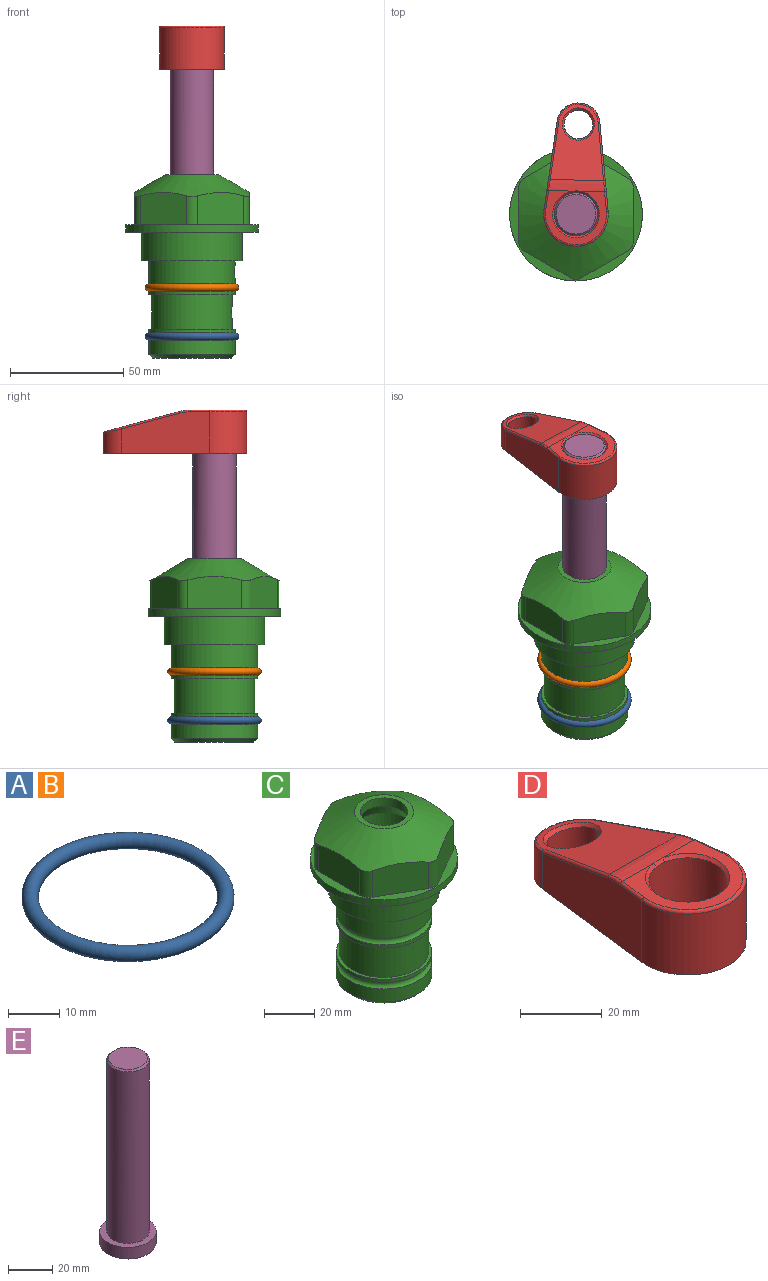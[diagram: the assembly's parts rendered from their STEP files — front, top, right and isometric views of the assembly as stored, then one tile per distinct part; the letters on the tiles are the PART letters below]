
ASSEMBLY  parts=5 mates=4
PART A: 1 faces, bbox 44.7x44.7x3.2 mm
  f0: torus R=19.05mm, axis (0,0,1), area 1193.9mm2
PART B: same geometry as A
PART C: 36 faces, bbox 58.7x58.7x81 mm
  f0: cylinder r=17.78mm len=35.56mm, axis (0,0,1), area 1670.8mm2, adj f23,f24,f31
  f1: cylinder r=19.05mm len=38.1mm, axis (0,0,1), area 1191.9mm2, adj f26,f27,f30
  f2: plane 58.66x58.66mm, normal (0,0,-1), area 1150.6mm2, adj f3,f28
  f3: cylinder r=29.33mm len=58.66mm, axis (0,0,-1), area 585.1mm2, adj f2,f4
  f4: plane 58.66x58.66mm, normal (0,0,1), area 475.9mm2, adj f3,f5,f6,f7,f8,f9,f10,f11
  f5: plane 20.32x14.34mm, normal (-0.5,0.87,0), area 324.4mm2, adj f4,f15,f16,f17
  f6: plane 20.32x14.34mm, normal (0.5,0.87,0), area 324.4mm2, adj f4,f14,f15,f17
  f7: plane 23.48x14.34mm, normal (1,0,0), area 324.4mm2, adj f4,f13,f14,f17
  f8: plane 20.32x14.34mm, normal (0.5,-0.87,0), area 324.4mm2, adj f4,f12,f13,f17
  f9: plane 20.32x14.34mm, normal (-0.5,-0.87,0), area 324.4mm2, adj f4,f11,f12,f17
  f10: plane 23.48x14.34mm, normal (-1,0,0), area 324.4mm2, adj f4,f11,f16,f17
  f11: cylinder r=5.08mm len=12.85mm, axis (0,0,-1), area 67.2mm2, adj f4,f9,f10,f17
  f12: cylinder r=5.08mm len=12.85mm, axis (0,0,-1), area 67.2mm2, adj f4,f8,f9,f17
  f13: cylinder r=5.08mm len=12.85mm, axis (0,0,-1), area 67.2mm2, adj f4,f7,f8,f17
  f14: cylinder r=5.08mm len=12.85mm, axis (0,0,-1), area 67.2mm2, adj f4,f6,f7,f17
  f15: cylinder r=5.08mm len=12.85mm, axis (0,0,-1), area 67.2mm2, adj f4,f5,f6,f17
  f16: cylinder r=5.08mm len=12.85mm, axis (0,0,-1), area 67.2mm2, adj f4,f5,f10,f17
  f17: cone r=11.73mm half-angle=60deg, axis (0,0,-1), area 2071.8mm2, adj f5,f6,f7,f8,f9,f10,f11,f12
  f18: plane 23.46x23.46mm, normal (0,0,1), area 147.4mm2, adj f17,f35
  f19: plane 34.93x34.93mm, normal (0,0,-1), area 958mm2, adj f29
  f20: cylinder r=19.05mm len=38.1mm, axis (0,0,1), area 760.1mm2, adj f21,f29
  f21: torus R=19.05mm, axis (0,0,1), area 565.3mm2, adj f20,f22
  f22: cylinder r=19.05mm len=38.1mm, axis (0,0,1), area 190mm2, adj f21,f23
  f23: plane 38.1x38.1mm, normal (0,0,1), area 146.9mm2, adj f0,f22
  f24: plane 38.1x38.1mm, normal (0,0,-1), area 146.9mm2, adj f0,f25
  f25: cylinder r=19.05mm len=38.1mm, axis (0,0,1), area 190mm2, adj f24,f26
  f26: torus R=19.05mm, axis (0,0,1), area 565.3mm2, adj f1,f25
  f27: plane 44.45x44.45mm, normal (0,0,-1), area 411.7mm2, adj f1,f28
  f28: cylinder r=22.23mm len=44.45mm, axis (0,0,1), area 1773.5mm2, adj f2,f27
  f29: cone r=19.05mm half-angle=45deg, axis (0,0,1), area 257.5mm2, adj f19,f20
  f30: cylinder r=3.17mm len=6.75mm, axis (-1,0,0), area 128mm2, adj f1,f33
  f31: cylinder r=3.17mm len=6.35mm, axis (-1,0,0), area 102.5mm2, adj f0,f33
  f32: plane 25.4x25.4mm, normal (0,0,1), area 506.7mm2, adj f33
  f33: cylinder r=12.7mm len=66.42mm, axis (0,0,-1), area 5236.2mm2, adj f30,f31,f32,f34
  f34: cone r=9.53mm half-angle=30deg, axis (0,0,-1), area 443.4mm2, adj f33,f35
  f35: cylinder r=9.53mm len=19.05mm, axis (0,0,-1), area 240.9mm2, adj f18,f34
PART D: 31 faces, bbox 31.7x65.5x19.8 mm
  f0: plane 39.12x18.26mm, normal (0.99,0.12,0), area 612.2mm2, adj f1,f4,f7,f11,f13,f15
  f1: cylinder r=9.53mm len=18.91mm, axis (0,0,-1), area 296.1mm2, adj f0,f2,f7,f17
  f2: plane 39.12x18.26mm, normal (-0.99,0.12,0), area 612.2mm2, adj f1,f4,f7,f12,f14,f16
  f3: cylinder r=6.35mm len=12.7mm, axis (0,0,-1), area 362.4mm2, adj f7,f18
  f4: cylinder r=14.29mm len=28.58mm, axis (0,0,-1), area 882.2mm2, adj f0,f2,f7,f10
  f5: cylinder r=9.53mm len=19.05mm, axis (0,0,-1), area 1092.6mm2, adj f7,f19,f20
  f6: plane 26.99x23.69mm, normal (0,0,1), area 216.2mm2, adj f9,f10,f11,f12,f19
  f7: plane 63.5x28.58mm, normal (0,0,-1), area 661.8mm2, adj f0,f1,f2,f3,f4,f5,f22,f23
  f8: plane 33.52x23.6mm, normal (0,0.26,0.97), area 486mm2, adj f9,f15,f16,f17,f18
  f9: cylinder r=19.05mm len=24.72mm, axis (1,0,0), area 120.4mm2, adj f6,f8,f13,f14,f20
  f10: torus R=13.49mm, axis (0,0,1), area 59mm2, adj f4,f6,f11,f12
  f11: cylinder r=0.79mm len=8.67mm, axis (0.12,-0.99,0), area 10.8mm2, adj f0,f6,f10,f13
  f12: cylinder r=0.79mm len=8.67mm, axis (0.12,0.99,0), area 10.8mm2, adj f2,f6,f10,f14
  f13: bspline ~4.95x1.42mm, area 6.1mm2, adj f0,f9,f11,f15
  f14: bspline ~4.95x1.42mm, area 6.1mm2, adj f2,f9,f12,f16
  f15: cylinder r=0.79mm len=25.95mm, axis (0.12,-0.96,0.26), area 32.9mm2, adj f0,f8,f13,f17
  f16: cylinder r=0.79mm len=25.95mm, axis (0.12,0.96,-0.26), area 32.9mm2, adj f2,f8,f14,f17
  f17: bspline ~18.91x8.38mm, area 30mm2, adj f1,f8,f15,f16
  f18: bspline ~14.29x14.29mm, area 48.3mm2, adj f3,f8
  f19: cone r=9.53mm half-angle=45deg, axis (0,0,1), area 66.5mm2, adj f5,f6,f20
  f20: bspline ~3.22x0.96mm, area 3.5mm2, adj f5,f9,f19
  f21: plane 2.75x2.72mm, normal (0,0,-1), area 2.9mm2, adj f23,f25,f28
  f22: plane 23.05x15.88mm, normal (-0.99,-0.12,0), area 323.6mm2, adj f7,f25,f26,f27,f28,f29
  f23: plane 23.05x15.88mm, normal (0.99,-0.12,0), area 323.6mm2, adj f7,f21,f25,f27,f28,f30
  f24: cylinder r=9.53mm len=10.69mm, axis (0,0,-1), area 114.7mm2, adj f7,f27,f29,f30
  f25: cylinder r=12.7mm len=20.59mm, axis (0,0,-1), area 381.1mm2, adj f7,f21,f22,f23,f26,f28
  f26: plane 2.75x2.72mm, normal (0,0,-1), area 2.9mm2, adj f22,f25,f28
  f27: plane 19.72x18.37mm, normal (0,-0.26,-0.97), area 291.8mm2, adj f22,f23,f24,f28,f29,f30
  f28: cylinder r=15.88mm len=19.92mm, axis (1,0,0), area 54.8mm2, adj f21,f22,f23,f25,f26,f27
  f29: cylinder r=1.59mm len=11mm, axis (0,0,-1), area 34.7mm2, adj f7,f22,f24,f27
  f30: cylinder r=1.59mm len=11mm, axis (0,0,-1), area 34.7mm2, adj f7,f23,f24,f27
PART E: 6 faces, bbox 25.4x25.4x101.6 mm
  f0: plane 17.46x17.46mm, normal (0,0,1), area 239.5mm2, adj f5
  f1: plane 25.4x25.4mm, normal (0,0,-1), area 506.7mm2, adj f2
  f2: cylinder r=12.7mm len=25.4mm, axis (0,0,1), area 506.7mm2, adj f1,f3
  f3: plane 25.4x25.4mm, normal (0,0,1), area 221.7mm2, adj f2,f4
  f4: cylinder r=9.53mm len=94.46mm, axis (0,0,1), area 5653mm2, adj f3,f5
  f5: cone r=8.73mm half-angle=45deg, axis (0,0,-1), area 64.4mm2, adj f0,f4
PLACE A t=(0,0,-21.59)mm
PLACE B at identity
PLACE C at identity fixed
PLACE D rot(axis=(0,0,-1),1.5deg) t=(0,0,27.55)mm
PLACE E rot(axis=(0,0,-1),1.5deg) t=(0,0,27.55)mm
MATE fastened C.f0 <-> B.f0  axis (0,0,1) through (0,0,-24.51)mm
MATE fastened C.f0 <-> A.f0  axis (0,0,1) through (0,0,-46.1)mm
MATE fastened E.f2 <-> D.f4  axis (0,0,1) through (0,0,91.05)mm
MATE cylindrical E.f2 <-> C.f0  axis (0,0,-1) through (0,0,-10.55)mm
